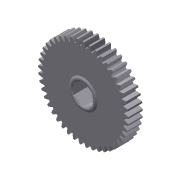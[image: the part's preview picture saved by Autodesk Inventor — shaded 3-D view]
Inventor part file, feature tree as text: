
AUTODESK INVENTOR PART (.ipt)
format: ipt  version: 2013 (Build 170138000, 138)  size: 377,856 bytes
history: native  units: mm (DEFAULTED — no unit token found)
features: sketch x5, extrude x3, plane x3, other x3, revolve x1, projected_geometry x1
ambient origin geometry x8: Origin, YZ Plane, XZ Plane, XY Plane, X Axis, Y Axis, Z Axis, Center Point
bodies: Solid1 (feature_tree)
feature tree (16):
  extrude  "Extrusion1"  Depth=9.525mm TaperAngle=0.0deg
  plane  "Work Plane1"
  plane  "Work Plane2"
  plane  "Work Plane3"
  other  "Spur Gear"
  extrude  "Extrusion2"  Depth=76.2mm TaperAngle=0.0deg
  extrude  "Extrusion3"  Depth=19.05mm
  revolve  "Revolution1"  [1 undecoded]
  sketch  "Sketch1"  dims[d0=59.69mm d1=9.525mm d2=0.0mm]
  sketch  "Sketch2"  dims[d3=57.15mm d4=76.2mm d5=0.0mm]
  other  "Srf1"
  sketch  "Sketch3"  dims[d6=0.0mm d7=0.698132mm d20=19.05mm]
  sketch  "Sketch4"  dims[d21=0.635mm d22=0.0mm d23=12.7mm]
  sketch  "Sketch5"  dims[d24=0.635mm d25=0.0mm d26=1.143mm d27=0.889mm d28=5.070181mm d29=2.54mm d30=90.0deg]
  other  "Pitch Diameter"
  projected_geometry  "Project Cut Edges1"
note: 1 required parameter value undecoded (feature->parameter linkage not recoverable at this tier; creation-order binding heuristic only, values carry confidence <= 0.55)
